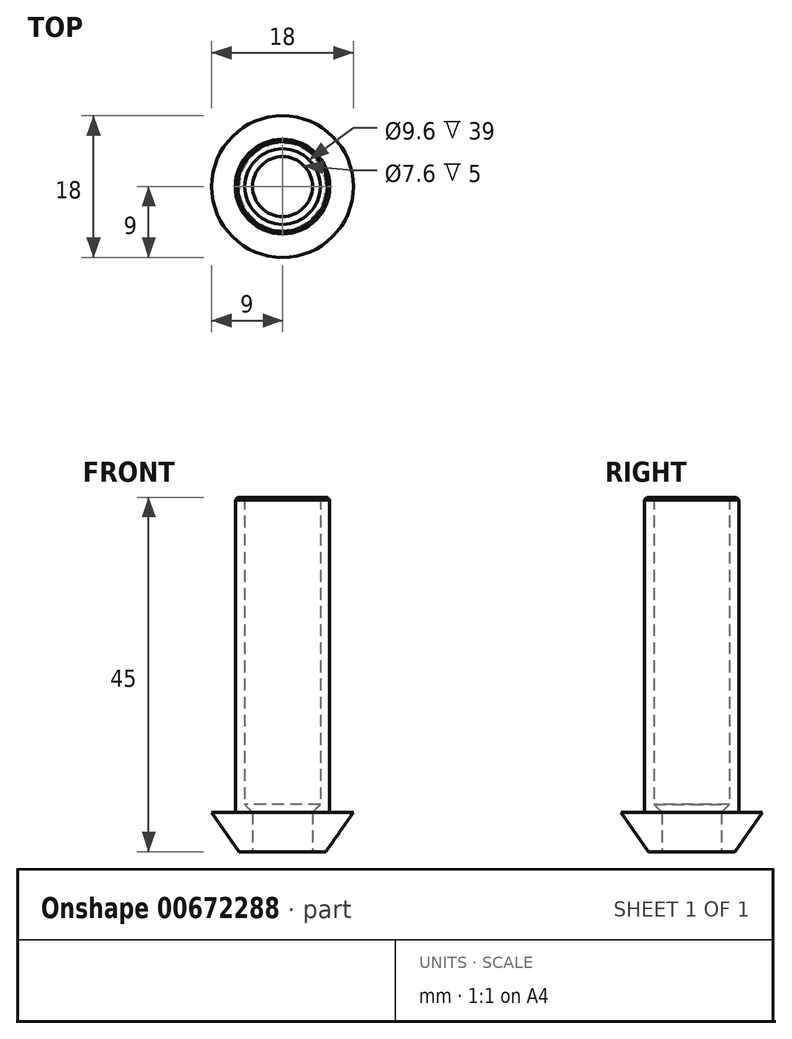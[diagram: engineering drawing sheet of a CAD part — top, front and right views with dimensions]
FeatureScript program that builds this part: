
annotation { "Feature Type Name" : "Feature", "Feature Type Description" : "" }
export const myFeature = defineFeature(function(context is Context, id is Id, definition is map)
    precondition{}
    {
        {
            var Q0;
            Q0=qCreatedBy(makeId("Top.planeOp"),FACE);
            var sketch = newSketch(context, id + "F0", { "sketchPlane" : qUnion([Q0])});
            skCircle(sketch, "E0", {"center": v(0, 0) * mm, "radius": 4.8 * mm});
            skCircle(sketch, "E1", {"center": v(0, 0) * mm, "radius": 6 * mm});
            skSolve(sketch);
        }
        {
            var Q0;
            Q0 = qSketchRegion(id + "F0", true);
            extrude(context, id + "F1", {"entities" : qUnion([Q0]), "depth" : 40 * mm, "offsetDistance" : 25 * mm});
        }
        {
            var Q0;
            Q0=qCreatedBy(makeId("Top.planeOp"),FACE);
            var sketch = newSketch(context, id + "F2", { "sketchPlane" : qUnion([Q0])});
            skCircle(sketch, "E2", {"center": v(0, 0) * mm, "radius": 9 * mm});
            skSolve(sketch);
        }
        {
            var Q0;
            Q0 = qSketchRegion(id + "F2", true);
            extrude(context, id + "F3", {"entities" : qUnion([Q0]), "operationType" : NewBodyOperationType.ADD, "oppositeDirection" : true, "depth" : 5 * mm, "offsetDistance" : 25 * mm, "hasDraft" : true, "draftAngle" : 35 * degree, "draftPullDirection" : true});
        }
        {
            var Q0;
            Q0=makeQuery(id+"F1.opExtrude","CAP_EDGE",EDGE,{"disambiguationData":[OSD([sQuery(id+"F0.wireOp",EDGE,"E0")])],"isStart":true});
            chamfer(context, id + "F4", {"entities" : qUnion([Q0]), "width" : 1 * mm, "tangentPropagation" : true});
        }
        {
            var Q0;
            Q0=makeQuery(id+"F1.opExtrude","CAP_EDGE",EDGE,{"disambiguationData":[OSD([sQuery(id+"F0.wireOp",EDGE,"E1")])],"isStart":false});
            chamfer(context, id + "F5", {"entities" : qUnion([Q0]), "width" : .3 * mm, "tangentPropagation" : true});
        }
        {
            var Q0;
            Q0=makeQuery(id+"F3.opExtrude","CAP_FACE",FACE,{"disambiguationData":[OSD([sQuery(id+"F2.wireOp",EDGE,"E2")])],"isStart":false});
            var sketch = newSketch(context, id + "F6", { "sketchPlane" : qUnion([Q0])});
            skCircle(sketch, "E3", {"center": v(0, 0) * mm, "radius": 3.8 * mm});
            skSolve(sketch);
        }
        {
            var Q0;
            Q0 = qSketchRegion(id + "F6", true);
            extrude(context, id + "F7", {"entities" : qUnion([Q0]), "operationType" : NewBodyOperationType.REMOVE, "oppositeDirection" : true, "depth" : 100 * mm, "offsetDistance" : 25 * mm});
        }
    });
